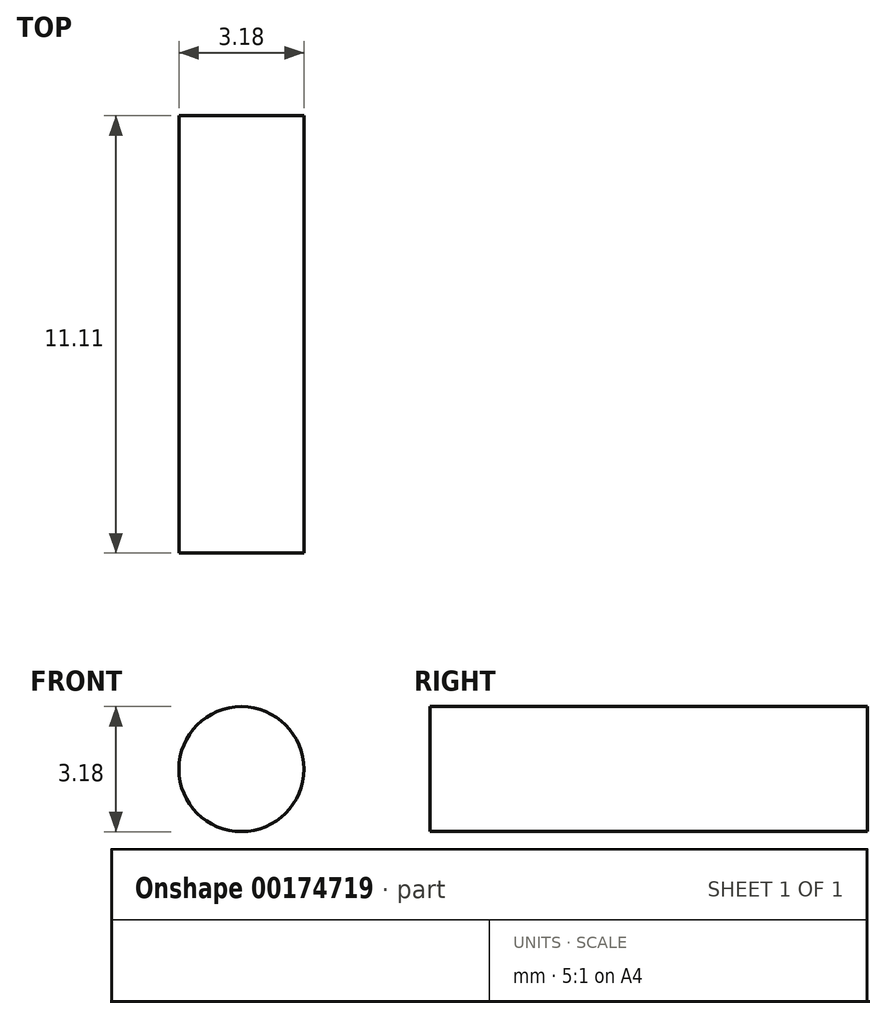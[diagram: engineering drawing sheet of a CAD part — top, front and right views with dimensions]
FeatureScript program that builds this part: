
annotation { "Feature Type Name" : "Feature", "Feature Type Description" : "" }
export const myFeature = defineFeature(function(context is Context, id is Id, definition is map)
    precondition{}
    {
        {
            var Q0;
            Q0=qCreatedBy(makeId("Front.planeOp"),FACE);
            var sketch = newSketch(context, id + "F0", { "sketchPlane" : qUnion([Q0])});
            skCircle(sketch, "E0", {"center": v(0, 0) * mm, "radius": 1.59 * mm});
            skSolve(sketch);
        }
        {
            var Q0;
            Q0=makeQuery(id+"F0.imprint","IMPRINT",FACE,{"disambiguationData":[TD([[makeQuery(id+"F0.imprint","IMPRINT",EDGE,{"derivedFrom":sQuery(id+"F0.wireOp",EDGE,"E0")}),1.0]])]});
            extrude(context, id + "F1", {"entities" : qUnion([Q0]), "depth" : 11.1 * mm});
        }
    });
